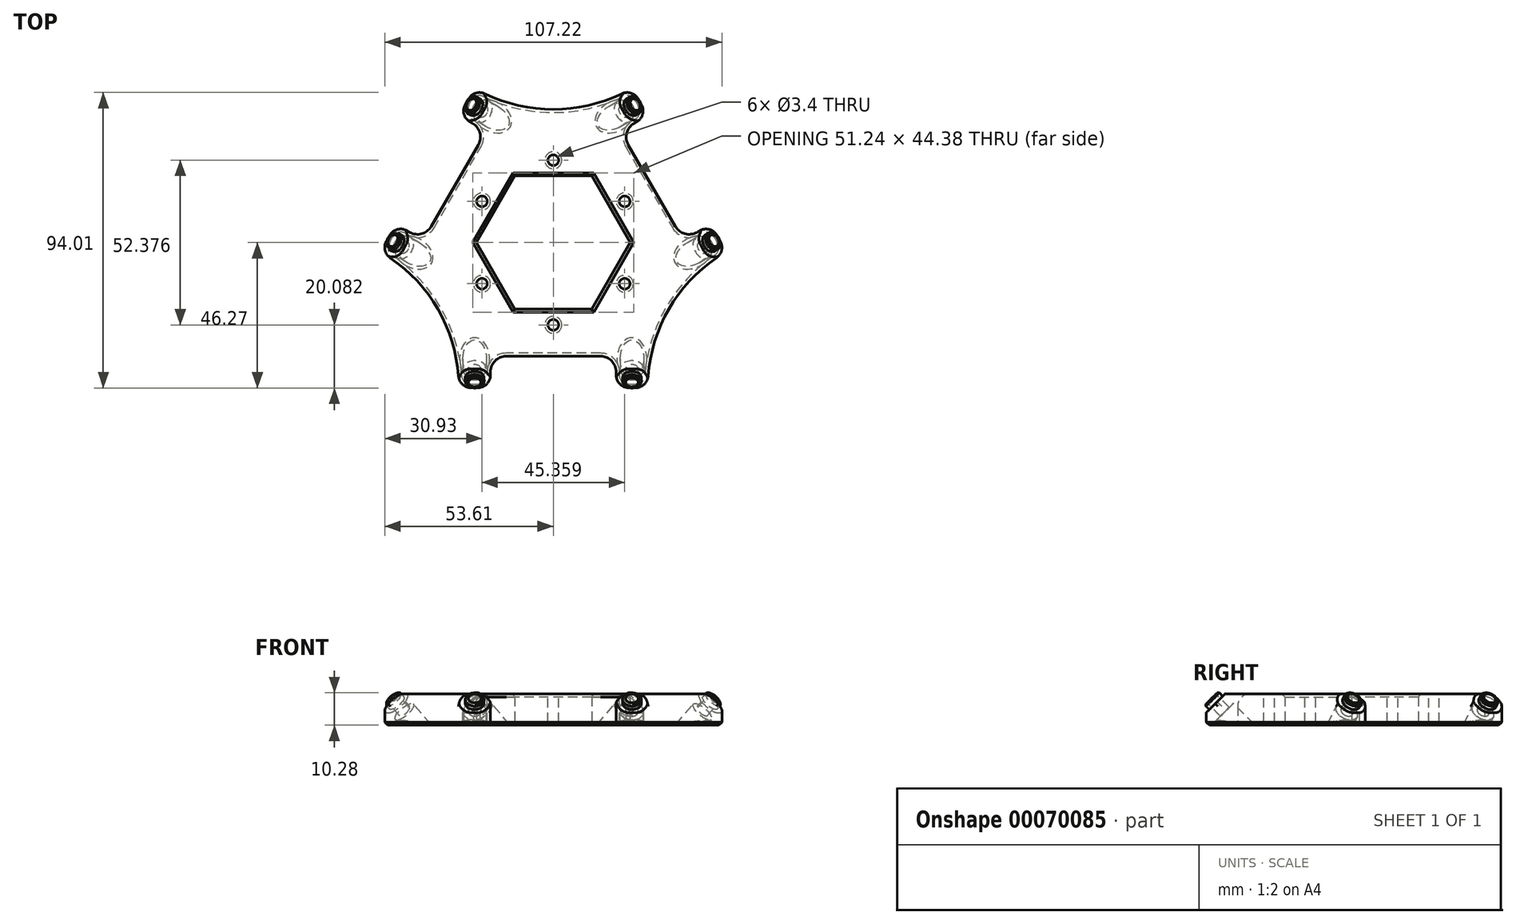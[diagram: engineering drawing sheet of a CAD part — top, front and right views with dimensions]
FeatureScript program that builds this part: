
annotation { "Feature Type Name" : "Feature", "Feature Type Description" : "" }
export const myFeature = defineFeature(function(context is Context, id is Id, definition is map)
    precondition{}
    {
        {
            var Q0;
            Q0=qCreatedBy(makeId("Top.planeOp"),FACE);
            var sketch = newSketch(context, id + "F0", { "sketchPlane" : qUnion([Q0])});
            skLineSegment(sketch, "E0", {"start": v(-55, -2.89) * mm, "end": v(-50, 5.77) * mm});
            skLineSegment(sketch, "E1", {"start": v(25, 49.07) * mm, "end": v(30, 40.41) * mm});
            skLineSegment(sketch, "E2", {"start": v(-30, -46.19) * mm, "end": v(-20, -46.19) * mm});
            skLineSegment(sketch, "E3", {"start": v(-25, 49.07) * mm, "end": v(0, 49.07) * mm, "construction": true});
            skLineSegment(sketch, "E4", {"start": v(0, 49.07) * mm, "end": v(25, 49.07) * mm, "construction": true});
            skLineSegment(sketch, "E5", {"start": v(30, -46.19) * mm, "end": v(42.5, -24.54) * mm, "construction": true});
            skLineSegment(sketch, "E6", {"start": v(42.5, -24.54) * mm, "end": v(55, -2.89) * mm, "construction": true});
            skLineSegment(sketch, "E7", {"start": v(0, 49.07) * mm, "end": v(0, -46.19) * mm, "construction": true});
            skArc(sketch, "E8", {"start": v(-30, -46.19) * mm, "mid": v(-36.7, -21.19) * mm, "end": v(-55, -2.89) * mm});
            skArc(sketch, "E9", {"start": v(-25, 49.07) * mm, "mid": v(0, 42.38) * mm, "end": v(25, 49.07) * mm});
            skArc(sketch, "E10", {"start": v(55, -2.89) * mm, "mid": v(36.7, -21.19) * mm, "end": v(30, -46.19) * mm});
            skLineSegment(sketch, "E11", {"start": v(-40, 23.1) * mm, "end": v(42.5, -24.54) * mm, "construction": true});
            skLineSegment(sketch, "E12", {"start": v(-50, 5.77) * mm, "end": v(-41.34, 0.77) * mm});
            skLineSegment(sketch, "E13", {"start": v(-41.34, 0.77) * mm, "end": v(-21.34, 35.41) * mm});
            skLineSegment(sketch, "E14", {"start": v(-21.34, 35.41) * mm, "end": v(-30, 40.41) * mm});
            skLineSegment(sketch, "E15", {"start": v(30, 40.41) * mm, "end": v(21.34, 35.41) * mm});
            skLineSegment(sketch, "E16", {"start": v(21.34, 35.41) * mm, "end": v(41.34, 0.77) * mm});
            skLineSegment(sketch, "E17", {"start": v(41.34, 0.77) * mm, "end": v(50, 5.77) * mm});
            skLineSegment(sketch, "E18", {"start": v(-20, -46.19) * mm, "end": v(-20, -36.19) * mm});
            skLineSegment(sketch, "E19", {"start": v(-20, -36.19) * mm, "end": v(20, -36.19) * mm});
            skLineSegment(sketch, "E20", {"start": v(20, -36.19) * mm, "end": v(20, -46.19) * mm});
            skLineSegment(sketch, "E21.trimOffspring", {"start": v(-30, 40.41) * mm, "end": v(-25, 49.07) * mm});
            skLineSegment(sketch, "E22.trimOffspring", {"start": v(50, 5.77) * mm, "end": v(55, -2.89) * mm});
            skLineSegment(sketch, "E23.trimOffspring", {"start": v(20, -46.19) * mm, "end": v(30, -46.19) * mm});
            skCircle(sketch, "E24.cCircle", {"center": v(0, 0) * mm, "radius": 24.47 * mm, "construction": true});
            skLineSegment(sketch, "E24.0", {"start": v(-12.23, 21.19) * mm, "end": v(12.23, 21.19) * mm});
            skLineSegment(sketch, "E24.1", {"start": v(12.23, 21.19) * mm, "end": v(24.47, 0) * mm});
            skLineSegment(sketch, "E24.2", {"start": v(24.47, 0) * mm, "end": v(12.23, -21.19) * mm});
            skLineSegment(sketch, "E24.3", {"start": v(12.23, -21.19) * mm, "end": v(-12.23, -21.19) * mm});
            skLineSegment(sketch, "E24.4", {"start": v(-12.23, -21.19) * mm, "end": v(-24.47, 0) * mm});
            skLineSegment(sketch, "E24.5", {"start": v(-24.47, 0) * mm, "end": v(-12.23, 21.19) * mm});
            skSolve(sketch);
        }
        {
            var Q0;
            Q0=makeQuery(id+"F0.imprint","IMPRINT",FACE,{"disambiguationData":[TD([[makeQuery(id+"F0.imprint","IMPRINT",EDGE,{"derivedFrom":sQuery(id+"F0.wireOp",EDGE,"E0")}),-1.0]])]});
            extrude(context, id + "F1", {"entities" : qUnion([Q0]), "depth" : 10 * mm, "offsetDistance" : 25 * mm});
        }
        {
            var Q0;
            Q0=makeQuery(id+"F1.opExtrude","SWEPT_EDGE",EDGE,{"disambiguationData":[OSD([sQuery(id+"F0.wireOp",EDGE,"E2"),sQuery(id+"F0.wireOp",EDGE,"E8")])]});
            var Q1;
            Q1=makeQuery(id+"F1.opExtrude","SWEPT_EDGE",EDGE,{"disambiguationData":[OSD([sQuery(id+"F0.wireOp",EDGE,"E2"),sQuery(id+"F0.wireOp",EDGE,"E18")])]});
            var Q2;
            Q2=makeQuery(id+"F1.opExtrude","SWEPT_EDGE",EDGE,{"disambiguationData":[OSD([sQuery(id+"F0.wireOp",EDGE,"E20"),sQuery(id+"F0.wireOp",EDGE,"E23.trimOffspring")])]});
            var Q3;
            Q3=makeQuery(id+"F1.opExtrude","SWEPT_EDGE",EDGE,{"disambiguationData":[OSD([sQuery(id+"F0.wireOp",EDGE,"E10"),sQuery(id+"F0.wireOp",EDGE,"E23.trimOffspring")])]});
            var Q4;
            Q4=makeQuery(id+"F1.opExtrude","SWEPT_EDGE",EDGE,{"disambiguationData":[OSD([sQuery(id+"F0.wireOp",EDGE,"E10"),sQuery(id+"F0.wireOp",EDGE,"E22.trimOffspring")])]});
            var Q5;
            Q5=makeQuery(id+"F1.opExtrude","SWEPT_EDGE",EDGE,{"disambiguationData":[OSD([sQuery(id+"F0.wireOp",EDGE,"E1"),sQuery(id+"F0.wireOp",EDGE,"E15")])]});
            var Q6;
            Q6=makeQuery(id+"F1.opExtrude","SWEPT_EDGE",EDGE,{"disambiguationData":[OSD([sQuery(id+"F0.wireOp",EDGE,"E14"),sQuery(id+"F0.wireOp",EDGE,"E21.trimOffspring")])]});
            var Q7;
            Q7=makeQuery(id+"F1.opExtrude","SWEPT_EDGE",EDGE,{"disambiguationData":[OSD([sQuery(id+"F0.wireOp",EDGE,"E0"),sQuery(id+"F0.wireOp",EDGE,"E8")])]});
            var Q8;
            Q8=makeQuery(id+"F1.opExtrude","SWEPT_EDGE",EDGE,{"disambiguationData":[OSD([sQuery(id+"F0.wireOp",EDGE,"E0"),sQuery(id+"F0.wireOp",EDGE,"E12")])]});
            var Q9;
            Q9=makeQuery(id+"F1.opExtrude","SWEPT_EDGE",EDGE,{"disambiguationData":[OSD([sQuery(id+"F0.wireOp",EDGE,"E9"),sQuery(id+"F0.wireOp",EDGE,"E21.trimOffspring")])]});
            var Q10;
            Q10=makeQuery(id+"F1.opExtrude","SWEPT_EDGE",EDGE,{"disambiguationData":[OSD([sQuery(id+"F0.wireOp",EDGE,"E1"),sQuery(id+"F0.wireOp",EDGE,"E9")])]});
            var Q11;
            Q11=makeQuery(id+"F1.opExtrude","SWEPT_EDGE",EDGE,{"disambiguationData":[OSD([sQuery(id+"F0.wireOp",EDGE,"E17"),sQuery(id+"F0.wireOp",EDGE,"E22.trimOffspring")])]});
            fillet(context, id + "F2", {"entities" : qUnion([Q0, Q1, Q2, Q3, Q4, Q5, Q6, Q7, Q8, Q9, Q10, Q11]), "radius" : 4 * mm, "tangentPropagation" : true, "allowEdgeOverflow" : false});
        }
        {
            var Q0;
            Q0=makeQuery(id+"F1.opExtrude","CAP_EDGE",EDGE,{"disambiguationData":[OSD([sQuery(id+"F0.wireOp",EDGE,"E2")])],"isStart":false});
            var Q1;
            Q1=makeQuery(id+"F1.opExtrude","CAP_EDGE",EDGE,{"disambiguationData":[OSD([sQuery(id+"F0.wireOp",EDGE,"E23.trimOffspring")])],"isStart":false});
            var Q2;
            Q2=makeQuery(id+"F1.opExtrude","CAP_EDGE",EDGE,{"disambiguationData":[OSD([sQuery(id+"F0.wireOp",EDGE,"E0")])],"isStart":false});
            var Q3;
            Q3=makeQuery(id+"F1.opExtrude","CAP_EDGE",EDGE,{"disambiguationData":[OSD([sQuery(id+"F0.wireOp",EDGE,"E21.trimOffspring")])],"isStart":false});
            var Q4;
            Q4=makeQuery(id+"F1.opExtrude","CAP_EDGE",EDGE,{"disambiguationData":[OSD([sQuery(id+"F0.wireOp",EDGE,"E1")])],"isStart":false});
            var Q5;
            Q5=makeQuery(id+"F1.opExtrude","CAP_EDGE",EDGE,{"disambiguationData":[OSD([sQuery(id+"F0.wireOp",EDGE,"E22.trimOffspring")])],"isStart":false});
            chamfer(context, id + "F3", {"entities" : qUnion([Q0, Q1, Q2, Q3, Q4, Q5]), "width" : 6 * mm});
        }
        {
            var Q0;
            Q0=makeQuery(id+"F3.opChamfer","BLEND_FACE",FACE,{"disambiguationData":[OSD([sQuery(id+"F0.wireOp",EDGE,"E2")])]});
            var sketch = newSketch(context, id + "F4", { "sketchPlane" : qUnion([Q0])});
            skCircle(sketch, "E25", {"center": v(-25, -25.45) * mm, "radius": 2 * mm});
            skPoint(sketch, "E25.centerSnap0", {"position": v(-25.18, -21.35) * mm});
            skCircle(sketch, "E26", {"center": v(-25, -25.45) * mm, "radius": 3 * mm});
            skCircle(sketch, "E27", {"center": v(-25, -25.45) * mm, "radius": 3.75 * mm});
            skCircle(sketch, "E28.1.0.0", {"center": v(25, -25.45) * mm, "radius": 3.75 * mm});
            skCircle(sketch, "E28.1.0.1", {"center": v(25, -25.45) * mm, "radius": 3 * mm});
            skCircle(sketch, "E28.1.0.2", {"center": v(25, -25.45) * mm, "radius": 2 * mm});
            skLineSegment(sketch, "E28.direction1", {"start": v(-25, -25.45) * mm, "end": v(25, -25.45) * mm, "construction": true});
            skLineSegment(sketch, "E29", {"start": v(-25, -25.45) * mm, "end": v(-25, -16.13) * mm, "construction": true});
            skLineSegment(sketch, "E30", {"start": v(-25, -21.35) * mm, "end": v(-20, -21.35) * mm, "construction": true});
            skLineSegment(sketch, "E31", {"start": v(25, -25.45) * mm, "end": v(25, -16.43) * mm, "construction": true});
            skLineSegment(sketch, "E32", {"start": v(25, -21.35) * mm, "end": v(20, -21.35) * mm, "construction": true});
            skSolve(sketch);
        }
        {
            var Q0;
            Q0 = qSketchRegion(id + "F4", true);
            var Q1;
            Q1=makeQuery(id+"F4.imprint","IMPRINT",FACE,{"disambiguationData":[TD([[makeQuery(id+"F4.imprint","IMPRINT",EDGE,{"derivedFrom":sQuery(id+"F4.wireOp",EDGE,"E25")}),-1.0]])]});
            var Q2;
            Q2=makeQuery(id+"F4.imprint","IMPRINT",FACE,{"disambiguationData":[TD([[makeQuery(id+"F4.imprint","IMPRINT",EDGE,{"derivedFrom":sQuery(id+"F4.wireOp",EDGE,"E28.1.0.1")}),1.0]])]});
            extrude(context, id + "F5", {"entities" : qUnion([Q0, Q1, Q2]), "operationType" : NewBodyOperationType.REMOVE, "oppositeDirection" : true, "depth" : 25 * mm, "offsetDistance" : 25 * mm, "hasSecondDirection" : true, "secondDirectionOppositeDirection" : true, "secondDirectionDepth" : 4 * mm});
        }
        {
            var Q0;
            Q0=makeQuery(id+"F4.imprint","IMPRINT",FACE,{"disambiguationData":[TD([[makeQuery(id+"F4.imprint","IMPRINT",EDGE,{"derivedFrom":sQuery(id+"F4.wireOp",EDGE,"E25")}),1.0]])]});
            var Q1;
            Q1=makeQuery(id+"F4.imprint","IMPRINT",FACE,{"disambiguationData":[TD([[makeQuery(id+"F4.imprint","IMPRINT",EDGE,{"derivedFrom":sQuery(id+"F4.wireOp",EDGE,"E28.1.0.2")}),1.0]])]});
            extrude(context, id + "F6", {"entities" : qUnion([Q0, Q1]), "operationType" : NewBodyOperationType.REMOVE, "oppositeDirection" : true, "depth" : 25 * mm, "offsetDistance" : 25 * mm});
        }
        {
            var Q0;
            Q0=makeQuery(id+"F4.imprint","IMPRINT",FACE,{"disambiguationData":[TD([[makeQuery(id+"F4.imprint","IMPRINT",EDGE,{"derivedFrom":sQuery(id+"F4.wireOp",EDGE,"E25")}),-1.0]])]});
            var Q1;
            Q1=makeQuery(id+"F4.imprint","IMPRINT",FACE,{"disambiguationData":[TD([[makeQuery(id+"F4.imprint","IMPRINT",EDGE,{"derivedFrom":sQuery(id+"F4.wireOp",EDGE,"E28.1.0.1")}),1.0]])]});
            extrude(context, id + "F7", {"entities" : qUnion([Q0, Q1]), "operationType" : NewBodyOperationType.ADD, "depth" : 2 * mm, "offsetDistance" : 25 * mm});
        }
        {
            var Q0;
            Q0=makeQuery(id+"F7.opExtrude","CAP_EDGE",EDGE,{"disambiguationData":[OSD([sQuery(id+"F4.wireOp",EDGE,"E26")])],"isStart":false});
            var Q1;
            Q1=makeQuery(id+"F7.opExtrude","CAP_EDGE",EDGE,{"disambiguationData":[OSD([sQuery(id+"F4.wireOp",EDGE,"E28.1.0.1")])],"isStart":false});
            chamfer(context, id + "F8", {"entities" : qUnion([Q0, Q1]), "width" : 0.5 * mm, "tangentPropagation" : true});
        }
        {
            var Q0;
            Q0=makeQuery(id+"F3.opChamfer","BLEND_FACE",FACE,{"disambiguationData":[OSD([sQuery(id+"F0.wireOp",EDGE,"E22.trimOffspring")])]});
            var sketch = newSketch(context, id + "F9", { "sketchPlane" : qUnion([Q0])});
            skCircle(sketch, "E33", {"center": v(3.9, 35.46) * mm, "radius": 2 * mm});
            skPoint(sketch, "E33.centerSnap0", {"position": v(35.52, -3.27) * mm});
            skCircle(sketch, "E34", {"center": v(3.9, 35.46) * mm, "radius": 3 * mm});
            skCircle(sketch, "E35", {"center": v(3.9, 35.46) * mm, "radius": 3.75 * mm});
            skCircle(sketch, "E36.1.0.0", {"center": v(35.52, -3.27) * mm, "radius": 3.75 * mm});
            skCircle(sketch, "E36.1.0.1", {"center": v(35.52, -3.27) * mm, "radius": 3 * mm});
            skCircle(sketch, "E36.1.0.2", {"center": v(35.52, -3.27) * mm, "radius": 2 * mm});
            skLineSegment(sketch, "E36.direction1", {"start": v(3.9, 35.46) * mm, "end": v(35.52, -3.27) * mm, "construction": true});
            skLineSegment(sketch, "E37", {"start": v(35.52, -3.27) * mm, "end": v(8.3, -25.5) * mm, "construction": true});
            skLineSegment(sketch, "E38", {"start": v(32.35, -5.86) * mm, "end": v(29.18, -2) * mm, "construction": true});
            skSolve(sketch);
        }
        {
            var Q0;
            Q0=makeQuery(id+"F9.imprint","IMPRINT",FACE,{"disambiguationData":[TD([[makeQuery(id+"F9.imprint","IMPRINT",EDGE,{"derivedFrom":sQuery(id+"F9.wireOp",EDGE,"E36.1.0.1")}),1.0]])]});
            var Q1;
            Q1=makeQuery(id+"F9.imprint","IMPRINT",FACE,{"disambiguationData":[TD([[makeQuery(id+"F9.imprint","IMPRINT",EDGE,{"derivedFrom":sQuery(id+"F9.wireOp",EDGE,"E36.1.0.0")}),1.0]])]});
            var Q2;
            Q2=makeQuery(id+"F9.imprint","IMPRINT",FACE,{"disambiguationData":[TD([[makeQuery(id+"F9.imprint","IMPRINT",EDGE,{"derivedFrom":sQuery(id+"F9.wireOp",EDGE,"E34")}),-1.0]])]});
            var Q3;
            Q3=makeQuery(id+"F9.imprint","IMPRINT",FACE,{"disambiguationData":[TD([[makeQuery(id+"F9.imprint","IMPRINT",EDGE,{"derivedFrom":sQuery(id+"F9.wireOp",EDGE,"E33")}),-1.0]])]});
            extrude(context, id + "F10", {"entities" : qUnion([Q0, Q1, Q2, Q3]), "operationType" : NewBodyOperationType.REMOVE, "oppositeDirection" : true, "depth" : 25 * mm, "offsetDistance" : 25 * mm, "hasSecondDirection" : true, "secondDirectionOppositeDirection" : true, "secondDirectionDepth" : 4 * mm});
        }
        {
            var Q0;
            Q0=makeQuery(id+"F9.imprint","IMPRINT",FACE,{"disambiguationData":[TD([[makeQuery(id+"F9.imprint","IMPRINT",EDGE,{"derivedFrom":sQuery(id+"F9.wireOp",EDGE,"E36.1.0.2")}),1.0]])]});
            var Q1;
            Q1=makeQuery(id+"F9.imprint","IMPRINT",FACE,{"disambiguationData":[TD([[makeQuery(id+"F9.imprint","IMPRINT",EDGE,{"derivedFrom":sQuery(id+"F9.wireOp",EDGE,"E33")}),1.0]])]});
            extrude(context, id + "F11", {"entities" : qUnion([Q0, Q1]), "operationType" : NewBodyOperationType.REMOVE, "oppositeDirection" : true, "depth" : 25 * mm, "offsetDistance" : 25 * mm});
        }
        {
            var Q0;
            Q0=makeQuery(id+"F9.imprint","IMPRINT",FACE,{"disambiguationData":[TD([[makeQuery(id+"F9.imprint","IMPRINT",EDGE,{"derivedFrom":sQuery(id+"F9.wireOp",EDGE,"E36.1.0.1")}),1.0]])]});
            var Q1;
            Q1=makeQuery(id+"F9.imprint","IMPRINT",FACE,{"disambiguationData":[TD([[makeQuery(id+"F9.imprint","IMPRINT",EDGE,{"derivedFrom":sQuery(id+"F9.wireOp",EDGE,"E33")}),-1.0]])]});
            extrude(context, id + "F12", {"entities" : qUnion([Q0, Q1]), "operationType" : NewBodyOperationType.ADD, "depth" : 2 * mm, "offsetDistance" : 25 * mm});
        }
        {
            var Q0;
            Q0=makeQuery(id+"F12.opExtrude","CAP_EDGE",EDGE,{"disambiguationData":[OSD([sQuery(id+"F9.wireOp",EDGE,"E36.1.0.1")])],"isStart":false});
            var Q1;
            Q1=makeQuery(id+"F12.opExtrude","CAP_EDGE",EDGE,{"disambiguationData":[OSD([sQuery(id+"F9.wireOp",EDGE,"E34")])],"isStart":false});
            chamfer(context, id + "F13", {"entities" : qUnion([Q0, Q1]), "width" : 0.5 * mm, "tangentPropagation" : true});
        }
        {
            var Q0;
            Q0=makeQuery(id+"F3.opChamfer","BLEND_FACE",FACE,{"disambiguationData":[OSD([sQuery(id+"F0.wireOp",EDGE,"E21.trimOffspring")])]});
            var sketch = newSketch(context, id + "F14", { "sketchPlane" : qUnion([Q0])});
            skCircle(sketch, "E39", {"center": v(-3.9, 35.46) * mm, "radius": 2 * mm});
            skCircle(sketch, "E40", {"center": v(-3.9, 35.46) * mm, "radius": 3 * mm});
            skCircle(sketch, "E41", {"center": v(-3.9, 35.46) * mm, "radius": 3.75 * mm});
            skCircle(sketch, "E42.1.0.0", {"center": v(-35.52, -3.27) * mm, "radius": 3.75 * mm});
            skCircle(sketch, "E42.1.0.1", {"center": v(-35.52, -3.27) * mm, "radius": 3 * mm});
            skCircle(sketch, "E42.1.0.2", {"center": v(-35.52, -3.27) * mm, "radius": 2 * mm});
            skLineSegment(sketch, "E42.direction1", {"start": v(-3.9, 35.46) * mm, "end": v(-35.52, -3.27) * mm, "construction": true});
            skLineSegment(sketch, "E43", {"start": v(-35.52, -3.27) * mm, "end": v(-30.54, -7.34) * mm, "construction": true});
            skLineSegment(sketch, "E44", {"start": v(-32.35, -5.86) * mm, "end": v(-29.18, -2) * mm, "construction": true});
            skSolve(sketch);
        }
        {
            var Q0;
            Q0=makeQuery(id+"F14.imprint","IMPRINT",FACE,{"disambiguationData":[TD([[makeQuery(id+"F14.imprint","IMPRINT",EDGE,{"derivedFrom":sQuery(id+"F14.wireOp",EDGE,"E40")}),-1.0]])]});
            var Q1;
            Q1=makeQuery(id+"F14.imprint","IMPRINT",FACE,{"disambiguationData":[TD([[makeQuery(id+"F14.imprint","IMPRINT",EDGE,{"derivedFrom":sQuery(id+"F14.wireOp",EDGE,"E39")}),-1.0]])]});
            var Q2;
            Q2=makeQuery(id+"F14.imprint","IMPRINT",FACE,{"disambiguationData":[TD([[makeQuery(id+"F14.imprint","IMPRINT",EDGE,{"derivedFrom":sQuery(id+"F14.wireOp",EDGE,"E42.1.0.0")}),1.0]])]});
            var Q3;
            Q3=makeQuery(id+"F14.imprint","IMPRINT",FACE,{"disambiguationData":[TD([[makeQuery(id+"F14.imprint","IMPRINT",EDGE,{"derivedFrom":sQuery(id+"F14.wireOp",EDGE,"E42.1.0.1")}),1.0]])]});
            extrude(context, id + "F15", {"entities" : qUnion([Q0, Q1, Q2, Q3]), "operationType" : NewBodyOperationType.REMOVE, "oppositeDirection" : true, "depth" : 25 * mm, "offsetDistance" : 25 * mm, "hasSecondDirection" : true, "secondDirectionOppositeDirection" : true, "secondDirectionDepth" : 4 * mm});
        }
        {
            var Q0;
            Q0=makeQuery(id+"F14.imprint","IMPRINT",FACE,{"disambiguationData":[TD([[makeQuery(id+"F14.imprint","IMPRINT",EDGE,{"derivedFrom":sQuery(id+"F14.wireOp",EDGE,"E39")}),1.0]])]});
            var Q1;
            Q1=makeQuery(id+"F14.imprint","IMPRINT",FACE,{"disambiguationData":[TD([[makeQuery(id+"F14.imprint","IMPRINT",EDGE,{"derivedFrom":sQuery(id+"F14.wireOp",EDGE,"E42.1.0.2")}),1.0]])]});
            extrude(context, id + "F16", {"entities" : qUnion([Q0, Q1]), "operationType" : NewBodyOperationType.REMOVE, "oppositeDirection" : true, "depth" : 25 * mm, "offsetDistance" : 25 * mm});
        }
        {
            var Q0;
            Q0=makeQuery(id+"F14.imprint","IMPRINT",FACE,{"disambiguationData":[TD([[makeQuery(id+"F14.imprint","IMPRINT",EDGE,{"derivedFrom":sQuery(id+"F14.wireOp",EDGE,"E39")}),-1.0]])]});
            var Q1;
            Q1=makeQuery(id+"F14.imprint","IMPRINT",FACE,{"disambiguationData":[TD([[makeQuery(id+"F14.imprint","IMPRINT",EDGE,{"derivedFrom":sQuery(id+"F14.wireOp",EDGE,"E42.1.0.1")}),1.0]])]});
            extrude(context, id + "F17", {"entities" : qUnion([Q0, Q1]), "operationType" : NewBodyOperationType.ADD, "depth" : 2 * mm, "offsetDistance" : 25 * mm});
        }
        {
            var Q0;
            Q0=makeQuery(id+"F17.opExtrude","CAP_EDGE",EDGE,{"disambiguationData":[OSD([sQuery(id+"F14.wireOp",EDGE,"E40")])],"isStart":false});
            var Q1;
            Q1=makeQuery(id+"F17.opExtrude","CAP_EDGE",EDGE,{"disambiguationData":[OSD([sQuery(id+"F14.wireOp",EDGE,"E42.1.0.1")])],"isStart":false});
            chamfer(context, id + "F18", {"entities" : qUnion([Q0, Q1]), "width" : 0.5 * mm, "tangentPropagation" : true});
        }
        {
            var Q0;
            Q0=makeQuery(id+"F1.opExtrude","SWEPT_EDGE",EDGE,{"disambiguationData":[OSD([sQuery(id+"F0.wireOp",EDGE,"E16"),sQuery(id+"F0.wireOp",EDGE,"E17")])]});
            var Q1;
            Q1=makeQuery(id+"F1.opExtrude","SWEPT_EDGE",EDGE,{"disambiguationData":[OSD([sQuery(id+"F0.wireOp",EDGE,"E15"),sQuery(id+"F0.wireOp",EDGE,"E16")])]});
            var Q2;
            Q2=makeQuery(id+"F1.opExtrude","SWEPT_EDGE",EDGE,{"disambiguationData":[OSD([sQuery(id+"F0.wireOp",EDGE,"E19"),sQuery(id+"F0.wireOp",EDGE,"E20")])]});
            var Q3;
            Q3=makeQuery(id+"F1.opExtrude","SWEPT_EDGE",EDGE,{"disambiguationData":[OSD([sQuery(id+"F0.wireOp",EDGE,"E18"),sQuery(id+"F0.wireOp",EDGE,"E19")])]});
            var Q4;
            Q4=makeQuery(id+"F1.opExtrude","SWEPT_EDGE",EDGE,{"disambiguationData":[OSD([sQuery(id+"F0.wireOp",EDGE,"E12"),sQuery(id+"F0.wireOp",EDGE,"E13")])]});
            var Q5;
            Q5=makeQuery(id+"F1.opExtrude","SWEPT_EDGE",EDGE,{"disambiguationData":[OSD([sQuery(id+"F0.wireOp",EDGE,"E13"),sQuery(id+"F0.wireOp",EDGE,"E14")])]});
            fillet(context, id + "F19", {"entities" : qUnion([Q0, Q1, Q2, Q3, Q4, Q5]), "radius" : 5 * mm, "tangentPropagation" : true, "allowEdgeOverflow" : false});
        }
        {
            var Q0;
            Q0=makeQuery(id+"F1.opExtrude","CAP_FACE",FACE,{"disambiguationData":[OSD([sQuery(id+"F0.wireOp",EDGE,"E0"),sQuery(id+"F0.wireOp",EDGE,"E1"),sQuery(id+"F0.wireOp",EDGE,"E2"),sQuery(id+"F0.wireOp",EDGE,"E8"),sQuery(id+"F0.wireOp",EDGE,"E9"),sQuery(id+"F0.wireOp",EDGE,"E10"),sQuery(id+"F0.wireOp",EDGE,"E12"),sQuery(id+"F0.wireOp",EDGE,"E13"),sQuery(id+"F0.wireOp",EDGE,"E14"),sQuery(id+"F0.wireOp",EDGE,"E15"),sQuery(id+"F0.wireOp",EDGE,"E16"),sQuery(id+"F0.wireOp",EDGE,"E17"),sQuery(id+"F0.wireOp",EDGE,"E18"),sQuery(id+"F0.wireOp",EDGE,"E19"),sQuery(id+"F0.wireOp",EDGE,"E20"),sQuery(id+"F0.wireOp",EDGE,"E21.trimOffspring"),sQuery(id+"F0.wireOp",EDGE,"E22.trimOffspring"),sQuery(id+"F0.wireOp",EDGE,"E23.trimOffspring"),sQuery(id+"F0.wireOp",EDGE,"E24.0"),sQuery(id+"F0.wireOp",EDGE,"E24.1"),sQuery(id+"F0.wireOp",EDGE,"E24.2"),sQuery(id+"F0.wireOp",EDGE,"E24.3"),sQuery(id+"F0.wireOp",EDGE,"E24.4"),sQuery(id+"F0.wireOp",EDGE,"E24.5")])],"isStart":false});
            var sketch = newSketch(context, id + "F20", { "sketchPlane" : qUnion([Q0])});
            skCircle(sketch, "E45", {"center": v(0, 26.19) * mm, "radius": 1.7 * mm});
            skCircle(sketch, "E46.1.0", {"center": v(-22.68, 13.1) * mm, "radius": 1.7 * mm});
            skCircle(sketch, "E46.2.0", {"center": v(-22.68, -13.1) * mm, "radius": 1.7 * mm});
            skCircle(sketch, "E46.3.0", {"center": v(0, -26.19) * mm, "radius": 1.7 * mm});
            skCircle(sketch, "E46.4.0", {"center": v(22.68, -13.1) * mm, "radius": 1.7 * mm});
            skCircle(sketch, "E46.5.0", {"center": v(22.68, 13.1) * mm, "radius": 1.7 * mm});
            skPoint(sketch, "E46.center", {"position": v(0, 0) * mm});
            skSolve(sketch);
        }
        {
            var Q0;
            Q0 = qSketchRegion(id + "F20", true);
            extrude(context, id + "F21", {"entities" : qUnion([Q0]), "operationType" : NewBodyOperationType.REMOVE, "oppositeDirection" : true, "depth" : 25 * mm, "offsetDistance" : 25 * mm});
        }
        {
            var Q0;
            Q0=makeQuery(id+"F1.opExtrude","CAP_EDGE",EDGE,{"disambiguationData":[OSD([sQuery(id+"F0.wireOp",EDGE,"E13")])],"isStart":false});
            var Q1;
            Q1=makeQuery(id+"F1.opExtrude","CAP_EDGE",EDGE,{"disambiguationData":[OSD([sQuery(id+"F0.wireOp",EDGE,"E16")])],"isStart":false});
            var Q2;
            Q2=makeQuery(id+"F1.opExtrude","CAP_EDGE",EDGE,{"disambiguationData":[OSD([sQuery(id+"F0.wireOp",EDGE,"E19")])],"isStart":false});
            var Q3;
            Q3=makeQuery(id+"F1.opExtrude","CAP_EDGE",EDGE,{"disambiguationData":[OSD([sQuery(id+"F0.wireOp",EDGE,"E10")])],"isStart":false});
            var Q4;
            Q4=makeQuery(id+"F1.opExtrude","CAP_EDGE",EDGE,{"disambiguationData":[OSD([sQuery(id+"F0.wireOp",EDGE,"E8")])],"isStart":false});
            var Q5;
            Q5=makeQuery(id+"F1.opExtrude","CAP_EDGE",EDGE,{"disambiguationData":[OSD([sQuery(id+"F0.wireOp",EDGE,"E9")])],"isStart":false});
            fillet(context, id + "F22", {"entities" : qUnion([Q0, Q1, Q2, Q3, Q4, Q5]), "radius" : 4 * mm, "tangentPropagation" : true, "allowEdgeOverflow" : false});
        }
        {
            var Q0;
            {var subQ0=sQuery(id+"F0.wireOp",EDGE,"E24.2");var subQ2=sQuery(id+"F0.wireOp",EDGE,"E24.1");var subQ4=sQuery(id+"F0.wireOp",EDGE,"E24.0");var subQ6=sQuery(id+"F0.wireOp",EDGE,"E23.trimOffspring");var subQ8=sQuery(id+"F0.wireOp",EDGE,"E22.trimOffspring");var subQ10=sQuery(id+"F0.wireOp",EDGE,"E21.trimOffspring");var subQ12=sQuery(id+"F0.wireOp",EDGE,"E20");var subQ14=sQuery(id+"F0.wireOp",EDGE,"E19");var subQ16=sQuery(id+"F0.wireOp",EDGE,"E18");var subQ18=sQuery(id+"F0.wireOp",EDGE,"E17");var subQ20=sQuery(id+"F0.wireOp",EDGE,"E16");var subQ22=sQuery(id+"F0.wireOp",EDGE,"E2");var subQ24=sQuery(id+"F0.wireOp",EDGE,"E1");var subQ26=sQuery(id+"F0.wireOp",EDGE,"E8");var subQ28=sQuery(id+"F0.wireOp",EDGE,"E24.3");var subQ30=sQuery(id+"F0.wireOp",EDGE,"E0");var subQ31=makeQuery(id+"F1.opExtrude","SWEPT_FACE",FACE,{"disambiguationData":[OSD([subQ30])]});var subQ32=sQuery(id+"F0.wireOp",EDGE,"E15");var subQ34=sQuery(id+"F0.wireOp",EDGE,"E9");var subQ36=sQuery(id+"F0.wireOp",EDGE,"E10");var subQ38=sQuery(id+"F0.wireOp",EDGE,"E12");var subQ40=sQuery(id+"F0.wireOp",EDGE,"E13");var subQ42=sQuery(id+"F0.wireOp",EDGE,"E14");var subQ44=sQuery(id+"F0.wireOp",EDGE,"E24.4");var subQ46=sQuery(id+"F0.wireOp",EDGE,"E24.5");Q0=makeQuery(id+"F15.boolean.opBoolean","SPLIT",FACE,{"disambiguationData":[TD([subQ31])],"derivedFrom":makeQuery(id+"F10.boolean.opBoolean","SPLIT",FACE,{"disambiguationData":[TD([subQ31])],"derivedFrom":makeQuery(id+"F5.boolean.opBoolean","SPLIT",FACE,{"disambiguationData":[TD([subQ31])],"derivedFrom":makeQuery(id+"F1.opExtrude","CAP_FACE",FACE,{"disambiguationData":[OSD([subQ30,subQ24,subQ22,subQ26,subQ34,subQ36,subQ38,subQ40,subQ42,subQ32,subQ20,subQ18,subQ16,subQ14,subQ12,subQ10,subQ8,subQ6,subQ4,subQ2,subQ0,subQ28,subQ44,subQ46])],"isStart":true})})})});}
            var Q1;
            Q1=makeQuery(id+"F1.opExtrude","CAP_EDGE",EDGE,{"disambiguationData":[OSD([sQuery(id+"F0.wireOp",EDGE,"E24.3")])],"isStart":false});
            var Q2;
            Q2=makeQuery(id+"F1.opExtrude","CAP_EDGE",EDGE,{"disambiguationData":[OSD([sQuery(id+"F0.wireOp",EDGE,"E24.2")])],"isStart":false});
            var Q3;
            Q3=makeQuery(id+"F1.opExtrude","CAP_EDGE",EDGE,{"disambiguationData":[OSD([sQuery(id+"F0.wireOp",EDGE,"E24.1")])],"isStart":false});
            var Q4;
            Q4=makeQuery(id+"F1.opExtrude","CAP_EDGE",EDGE,{"disambiguationData":[OSD([sQuery(id+"F0.wireOp",EDGE,"E24.0")])],"isStart":false});
            var Q5;
            Q5=makeQuery(id+"F1.opExtrude","CAP_EDGE",EDGE,{"disambiguationData":[OSD([sQuery(id+"F0.wireOp",EDGE,"E24.5")])],"isStart":false});
            var Q6;
            Q6=makeQuery(id+"F1.opExtrude","CAP_EDGE",EDGE,{"disambiguationData":[OSD([sQuery(id+"F0.wireOp",EDGE,"E24.4")])],"isStart":false});
            var Q7;
            Q7=makeQuery(id+"F21.boolean.opBoolean","COPY",EDGE,{"derivedFrom":makeQuery(id+"F21.opExtrude","CAP_EDGE",EDGE,{"disambiguationData":[OSD([sQuery(id+"F20.wireOp",EDGE,"E46.3.0")])],"isStart":true})});
            var Q8;
            Q8=makeQuery(id+"F21.boolean.opBoolean","COPY",EDGE,{"derivedFrom":makeQuery(id+"F21.opExtrude","CAP_EDGE",EDGE,{"disambiguationData":[OSD([sQuery(id+"F20.wireOp",EDGE,"E46.2.0")])],"isStart":true})});
            var Q9;
            Q9=makeQuery(id+"F21.boolean.opBoolean","COPY",EDGE,{"derivedFrom":makeQuery(id+"F21.opExtrude","CAP_EDGE",EDGE,{"disambiguationData":[OSD([sQuery(id+"F20.wireOp",EDGE,"E46.1.0")])],"isStart":true})});
            var Q10;
            Q10=makeQuery(id+"F21.boolean.opBoolean","COPY",EDGE,{"derivedFrom":makeQuery(id+"F21.opExtrude","CAP_EDGE",EDGE,{"disambiguationData":[OSD([sQuery(id+"F20.wireOp",EDGE,"E45")])],"isStart":true})});
            var Q11;
            Q11=makeQuery(id+"F21.boolean.opBoolean","COPY",EDGE,{"derivedFrom":makeQuery(id+"F21.opExtrude","CAP_EDGE",EDGE,{"disambiguationData":[OSD([sQuery(id+"F20.wireOp",EDGE,"E46.5.0")])],"isStart":true})});
            var Q12;
            Q12=makeQuery(id+"F21.boolean.opBoolean","COPY",EDGE,{"derivedFrom":makeQuery(id+"F21.opExtrude","CAP_EDGE",EDGE,{"disambiguationData":[OSD([sQuery(id+"F20.wireOp",EDGE,"E46.4.0")])],"isStart":true})});
            chamfer(context, id + "F23", {"entities" : qUnion([Q0, Q1, Q2, Q3, Q4, Q5, Q6, Q7, Q8, Q9, Q10, Q11, Q12]), "width" : 1 * mm, "tangentPropagation" : true});
        }
    });
